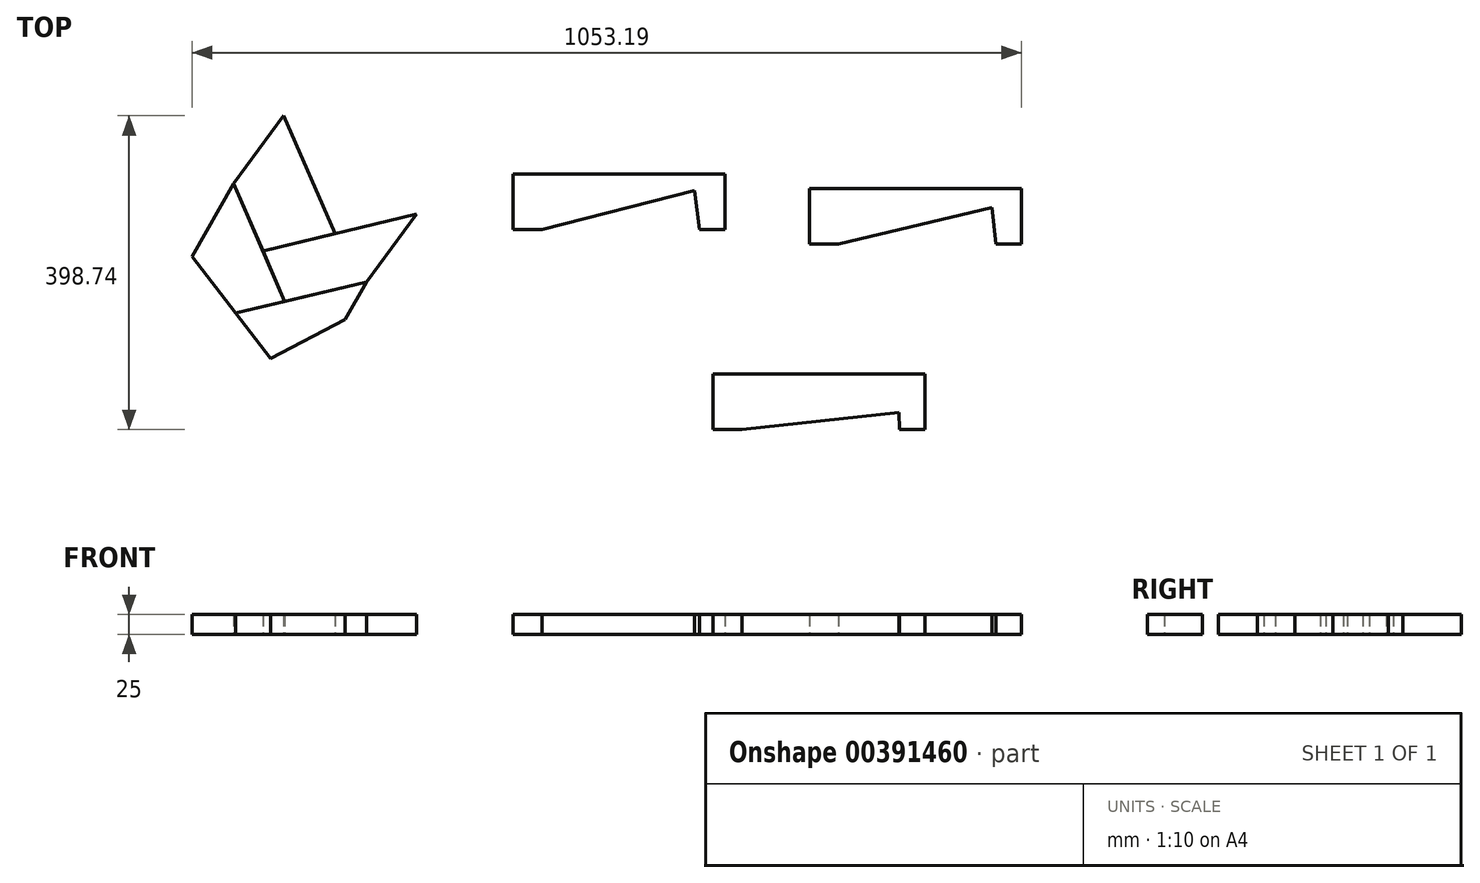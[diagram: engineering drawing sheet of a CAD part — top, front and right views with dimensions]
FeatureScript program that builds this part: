
annotation { "Feature Type Name" : "Feature", "Feature Type Description" : "" }
export const myFeature = defineFeature(function(context is Context, id is Id, definition is map)
    precondition{}
    {
        {
            var Q0;
            Q0=qCreatedBy(makeId("Top.planeOp"),FACE);
            var sketch = newSketch(context, id + "F0", { "sketchPlane" : qUnion([Q0])});
            skLineSegment(sketch, "E0", {"start": v(190.95, -1020.88) * mm, "end": v(-16.95, -991.23) * mm});
            skLineSegment(sketch, "E1", {"start": v(-16.95, -991.23) * mm, "end": v(11.16, -887.99) * mm});
            skLineSegment(sketch, "E2", {"start": v(11.16, -887.99) * mm, "end": v(205.4, -967.81) * mm});
            skLineSegment(sketch, "E3", {"start": v(205.4, -967.81) * mm, "end": v(190.95, -1020.88) * mm});
            skLineSegment(sketch, "E4", {"start": v(-2.9, -939.6) * mm, "end": v(198.17, -994.35) * mm, "construction": true});
            skLineSegment(sketch, "E5", {"start": v(232.44, -919.92) * mm, "end": v(63.77, -794.82) * mm});
            skLineSegment(sketch, "E6", {"start": v(63.77, -794.82) * mm, "end": v(127.52, -708.88) * mm});
            skLineSegment(sketch, "E7", {"start": v(127.52, -708.88) * mm, "end": v(296.19, -833.98) * mm});
            skLineSegment(sketch, "E8", {"start": v(296.19, -833.98) * mm, "end": v(232.44, -919.92) * mm});
            skLineSegment(sketch, "E9", {"start": v(95.65, -751.85) * mm, "end": v(264.31, -876.95) * mm, "construction": true});
            skLineSegment(sketch, "E10", {"start": v(205.4, -967.81) * mm, "end": v(11.16, -887.99) * mm});
            skLineSegment(sketch, "E11", {"start": v(11.16, -887.99) * mm, "end": v(63.77, -794.82) * mm});
            skLineSegment(sketch, "E12", {"start": v(63.77, -794.82) * mm, "end": v(232.44, -919.92) * mm});
            skLineSegment(sketch, "E13", {"start": v(232.44, -919.92) * mm, "end": v(205.4, -967.81) * mm});
            skLineSegment(sketch, "E14", {"start": v(37.47, -841.4) * mm, "end": v(218.92, -943.87) * mm, "construction": true});
            skLineSegment(sketch, "E15", {"start": v(-16.95, -991.23) * mm, "end": v(190.95, -1020.88) * mm});
            skSolve(sketch);
        }
        {
            var Q0;
            Q0=qCreatedBy(makeId("Top.planeOp"),FACE);
            var sketch = newSketch(context, id + "F1", { "sketchPlane" : qUnion([Q0])});
            skLineSegment(sketch, "E16", {"start": v(296.19, -833.98) * mm, "end": v(100.96, -880.62) * mm});
            skLineSegment(sketch, "E17", {"start": v(100.96, -880.62) * mm, "end": v(128.74, -944.7) * mm});
            skLineSegment(sketch, "E18", {"start": v(128.74, -944.7) * mm, "end": v(232.44, -919.92) * mm});
            skLineSegment(sketch, "E19", {"start": v(232.44, -919.92) * mm, "end": v(296.19, -833.98) * mm});
            skLineSegment(sketch, "E20", {"start": v(127.52, -708.88) * mm, "end": v(63.77, -794.82) * mm});
            skLineSegment(sketch, "E21", {"start": v(63.77, -794.82) * mm, "end": v(100.96, -880.62) * mm});
            skLineSegment(sketch, "E22", {"start": v(100.96, -880.62) * mm, "end": v(192.48, -858.75) * mm});
            skLineSegment(sketch, "E23", {"start": v(192.48, -858.75) * mm, "end": v(127.52, -708.88) * mm});
            skLineSegment(sketch, "E24", {"start": v(232.44, -919.92) * mm, "end": v(66.41, -959.58) * mm});
            skLineSegment(sketch, "E25", {"start": v(66.41, -959.58) * mm, "end": v(110.96, -1017.3) * mm});
            skLineSegment(sketch, "E26", {"start": v(110.96, -1017.3) * mm, "end": v(205.4, -967.81) * mm});
            skLineSegment(sketch, "E27", {"start": v(205.4, -967.81) * mm, "end": v(232.44, -919.92) * mm});
            skLineSegment(sketch, "E28", {"start": v(63.77, -794.82) * mm, "end": v(11.16, -887.99) * mm});
            skLineSegment(sketch, "E29", {"start": v(11.16, -887.99) * mm, "end": v(66.41, -959.58) * mm});
            skLineSegment(sketch, "E30", {"start": v(66.41, -959.58) * mm, "end": v(128.74, -944.7) * mm});
            skLineSegment(sketch, "E31", {"start": v(128.74, -944.7) * mm, "end": v(63.77, -794.82) * mm});
            skLineSegment(sketch, "E32", {"start": v(205.4, -967.81) * mm, "end": v(54.2, -1047.05) * mm});
            skLineSegment(sketch, "E33", {"start": v(54.2, -1047.05) * mm, "end": v(111.57, -1092.06) * mm});
            skLineSegment(sketch, "E34", {"start": v(111.57, -1092.06) * mm, "end": v(190.95, -1020.88) * mm});
            skLineSegment(sketch, "E35", {"start": v(190.95, -1020.88) * mm, "end": v(205.4, -967.81) * mm});
            skLineSegment(sketch, "E36", {"start": v(11.16, -887.99) * mm, "end": v(-16.95, -991.23) * mm});
            skLineSegment(sketch, "E37", {"start": v(-16.95, -991.23) * mm, "end": v(54.2, -1047.05) * mm});
            skLineSegment(sketch, "E38", {"start": v(54.2, -1047.05) * mm, "end": v(110.96, -1017.3) * mm});
            skLineSegment(sketch, "E39", {"start": v(110.96, -1017.3) * mm, "end": v(11.16, -887.99) * mm});
            skSolve(sketch);
        }
        {
            var Q0;
            Q0=qCreatedBy(makeId("Top.planeOp"),FACE);
            var sketch = newSketch(context, id + "F2", { "sketchPlane" : qUnion([Q0])});
            skLineSegment(sketch, "E40", {"start": v(455.64, -853.38) * mm, "end": v(468.82, -957.97) * mm});
            skLineSegment(sketch, "E41", {"start": v(468.82, -957.97) * mm, "end": v(665.7, -933.17) * mm});
            skLineSegment(sketch, "E42", {"start": v(665.7, -933.17) * mm, "end": v(649.4, -803.77) * mm});
            skLineSegment(sketch, "E43", {"start": v(649.4, -803.77) * mm, "end": v(455.64, -853.38) * mm});
            skLineSegment(sketch, "E44", {"start": v(455.64, -853.38) * mm, "end": v(687.84, -853.38) * mm});
            skLineSegment(sketch, "E45", {"start": v(687.84, -853.38) * mm, "end": v(687.84, -783.07) * mm});
            skLineSegment(sketch, "E46", {"start": v(687.84, -783.07) * mm, "end": v(418.6, -783.07) * mm});
            skLineSegment(sketch, "E47", {"start": v(418.6, -783.07) * mm, "end": v(418.6, -853.38) * mm});
            skLineSegment(sketch, "E48", {"start": v(418.6, -853.38) * mm, "end": v(455.64, -853.38) * mm});
            skLineSegment(sketch, "E49", {"start": v(455.64, -853.38) * mm, "end": v(455.64, -853.38) * mm});
            skPoint(sketch, "E50", {"position": v(655.64, -853.38) * mm});
            skLineSegment(sketch, "E51", {"start": v(832.14, -871.97) * mm, "end": v(844.44, -976.67) * mm});
            skLineSegment(sketch, "E52", {"start": v(844.44, -976.67) * mm, "end": v(1041.72, -953.5) * mm});
            skLineSegment(sketch, "E53", {"start": v(1041.72, -953.5) * mm, "end": v(1026.7, -825.62) * mm});
            skLineSegment(sketch, "E54", {"start": v(1026.7, -825.62) * mm, "end": v(832.14, -871.97) * mm});
            skLineSegment(sketch, "E55", {"start": v(832.14, -871.97) * mm, "end": v(1064.35, -871.97) * mm});
            skLineSegment(sketch, "E56", {"start": v(1064.35, -871.97) * mm, "end": v(1064.35, -801.67) * mm});
            skLineSegment(sketch, "E57", {"start": v(1064.35, -801.67) * mm, "end": v(795.1, -801.67) * mm});
            skLineSegment(sketch, "E58", {"start": v(795.1, -801.67) * mm, "end": v(795.1, -871.97) * mm});
            skLineSegment(sketch, "E59", {"start": v(795.1, -871.97) * mm, "end": v(832.14, -871.97) * mm});
            skLineSegment(sketch, "E60", {"start": v(832.14, -871.97) * mm, "end": v(832.14, -871.97) * mm});
            skPoint(sketch, "E61", {"position": v(1032.14, -871.97) * mm});
            skLineSegment(sketch, "E62", {"start": v(709.78, -1107.62) * mm, "end": v(715.5, -1212.89) * mm});
            skLineSegment(sketch, "E63", {"start": v(715.5, -1212.89) * mm, "end": v(914.9, -1202.07) * mm});
            skLineSegment(sketch, "E64", {"start": v(914.9, -1202.07) * mm, "end": v(908.6, -1085.99) * mm});
            skLineSegment(sketch, "E65", {"start": v(908.6, -1085.99) * mm, "end": v(709.78, -1107.62) * mm});
            skLineSegment(sketch, "E66", {"start": v(709.78, -1107.62) * mm, "end": v(941.98, -1107.62) * mm});
            skLineSegment(sketch, "E67", {"start": v(941.98, -1107.62) * mm, "end": v(941.98, -1037.32) * mm});
            skLineSegment(sketch, "E68", {"start": v(941.98, -1037.32) * mm, "end": v(672.74, -1037.32) * mm});
            skLineSegment(sketch, "E69", {"start": v(672.74, -1037.32) * mm, "end": v(672.74, -1107.62) * mm});
            skLineSegment(sketch, "E70", {"start": v(672.74, -1107.62) * mm, "end": v(709.78, -1107.62) * mm});
            skLineSegment(sketch, "E71", {"start": v(709.78, -1107.62) * mm, "end": v(709.78, -1107.62) * mm});
            skPoint(sketch, "E72", {"position": v(909.78, -1107.62) * mm});
            skSolve(sketch);
        }
        {
            var Q0;
            {var subQ4=sQuery(id+"F2.wireOp",EDGE,"E43");Q0=makeQuery(id+"F2.imprint","IMPRINT",FACE,{"disambiguationData":[TD([[makeQuery(id+"F2.imprint","IMPRINT",EDGE,{"derivedFrom":subQ4}),-1.0]])]});}
            extrude(context, id + "F3", {"entities" : qUnion([Q0]), "depth" : 25 * mm, "offsetDistance" : 25 * mm});
        }
        {
            var Q0;
            {var subQ4=sQuery(id+"F2.wireOp",EDGE,"E54");Q0=makeQuery(id+"F2.imprint","IMPRINT",FACE,{"disambiguationData":[TD([[makeQuery(id+"F2.imprint","IMPRINT",EDGE,{"derivedFrom":subQ4}),-1.0]])]});}
            extrude(context, id + "F4", {"entities" : qUnion([Q0]), "depth" : 25 * mm, "offsetDistance" : 25 * mm});
        }
        {
            var Q0;
            {var subQ4=sQuery(id+"F2.wireOp",EDGE,"E65");Q0=makeQuery(id+"F2.imprint","IMPRINT",FACE,{"disambiguationData":[TD([[makeQuery(id+"F2.imprint","IMPRINT",EDGE,{"derivedFrom":subQ4}),-1.0]])]});}
            extrude(context, id + "F5", {"entities" : qUnion([Q0]), "depth" : 25 * mm, "offsetDistance" : 25 * mm});
        }
        {
            var Q0;
            {var subQ0=sQuery(id+"F1.wireOp",EDGE,"E20");Q0=makeQuery(id+"F1.imprint","IMPRINT",FACE,{"disambiguationData":[TD([[makeQuery(id+"F1.imprint","IMPRINT",EDGE,{"derivedFrom":subQ0}),1.0]])]});}
            extrude(context, id + "F6", {"entities" : qUnion([Q0]), "depth" : 25 * mm, "offsetDistance" : 25 * mm});
        }
        {
            var Q0;
            Q0=makeQuery(id+"F1.imprint","IMPRINT",FACE,{"disambiguationData":[TD([[makeQuery(id+"F1.imprint","IMPRINT",EDGE,{"derivedFrom":sQuery(id+"F1.wireOp",EDGE,"E16")}),1.0]])]});
            extrude(context, id + "F7", {"entities" : qUnion([Q0]), "depth" : 25 * mm, "offsetDistance" : 25 * mm});
        }
        {
            var Q0;
            {var subQ1=sQuery(id+"F1.wireOp",EDGE,"E28");Q0=makeQuery(id+"F1.imprint","IMPRINT",FACE,{"disambiguationData":[TD([[makeQuery(id+"F1.imprint","IMPRINT",EDGE,{"derivedFrom":subQ1}),1.0]])]});}
            extrude(context, id + "F8", {"entities" : qUnion([Q0]), "depth" : 25 * mm, "offsetDistance" : 25 * mm});
        }
        {
            var Q0;
            Q0=makeQuery(id+"F1.imprint","IMPRINT",FACE,{"disambiguationData":[TD([[makeQuery(id+"F1.imprint","IMPRINT",EDGE,{"derivedFrom":sQuery(id+"F1.wireOp",EDGE,"E24")}),1.0]])]});
            extrude(context, id + "F9", {"entities" : qUnion([Q0]), "depth" : 25 * mm, "offsetDistance" : 25 * mm});
        }
    });
